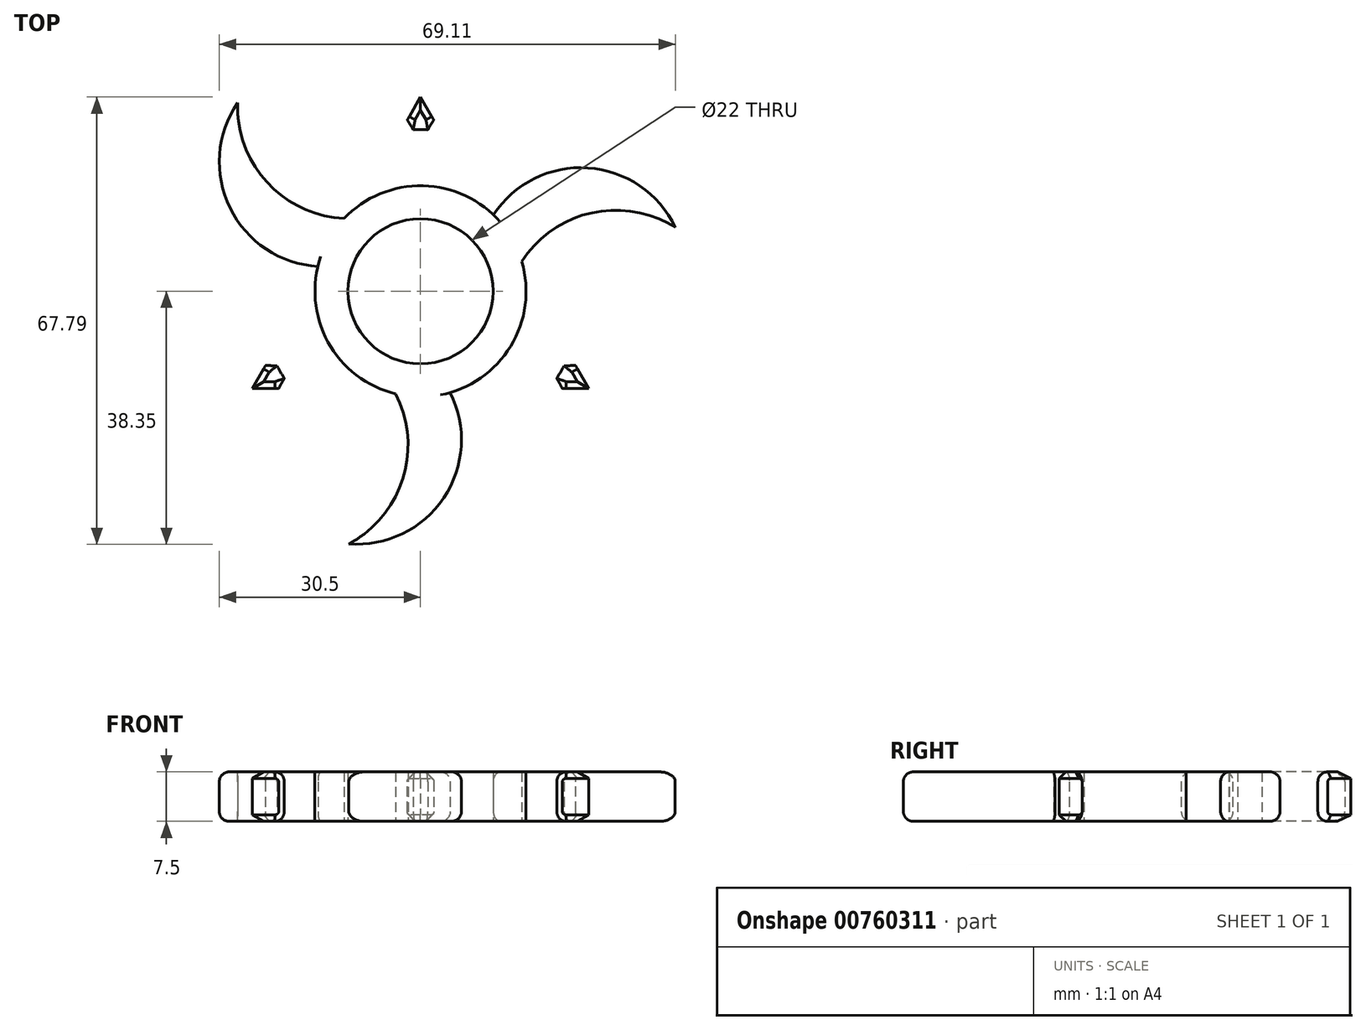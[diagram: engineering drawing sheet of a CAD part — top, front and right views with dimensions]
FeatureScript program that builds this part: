
annotation { "Feature Type Name" : "Feature", "Feature Type Description" : "" }
export const myFeature = defineFeature(function(context is Context, id is Id, definition is map)
    precondition{}
    {
        {
            var Q0;
            Q0=qCreatedBy(makeId("Top.planeOp"),FACE);
            var sketch = newSketch(context, id + "F0", { "sketchPlane" : qUnion([Q0])});
            skCircle(sketch, "E0", {"center": v(0, 0) * mm, "radius": 40 * mm, "construction": true});
            skLineSegment(sketch, "E1", {"start": v(-25.5, -14.72) * mm, "end": v(0, 29.44) * mm});
            skLineSegment(sketch, "E2", {"start": v(0, 29.44) * mm, "end": v(25.5, -14.72) * mm});
            skLineSegment(sketch, "E3", {"start": v(25.5, -14.72) * mm, "end": v(-25.5, -14.72) * mm});
            skCircle(sketch, "E4", {"center": v(0, 0) * mm, "radius": 11 * mm});
            skLineSegment(sketch, "E5", {"start": v(-25.5, -14.72) * mm, "end": v(0, 0) * mm, "construction": true});
            skLineSegment(sketch, "E6", {"start": v(0, 29.44) * mm, "end": v(0, 0) * mm, "construction": true});
            skLineSegment(sketch, "E7", {"start": v(0, 0) * mm, "end": v(25.5, -14.72) * mm, "construction": true});
            skCircle(sketch, "E8", {"center": v(0, 0) * mm, "radius": 16 * mm});
            skFitSpline(sketch, "E9", {"points": [v(7, -14.72) * mm, v(10.05, -23.38) * mm, v(9.77, -28.18) * mm, v(7.8, -33.41) * mm, v(4.12, -37.08) * mm, v(1.15, -38.78) * mm, v(-6.12, -39.53) * mm, v(-2.8, -36.94) * mm, v(2.56, -35.25) * mm, v(5.39, -31) * mm, v(2.14, -24.36) * mm, v(-7, -14.72) * mm], "startDerivative": vector(46.13, -62.16) * mm, "endDerivative": vector(-72.85, 54.12) * mm, "construction": true});
            skCircle(sketch, "E10", {"center": v(0, 0) * mm, "radius": 24.5 * mm});
            skCircle(sketch, "E11", {"center": v(0, 0) * mm, "radius": 20.5 * mm});
            skArc(sketch, "E12", {"start": v(-10.88, -38.3) * mm, "mid": v(3.51, -31.32) * mm, "end": v(4.5, -15.35) * mm});
            skArc(sketch, "E13.trimOffspring", {"start": v(-10.88, -38.3) * mm, "mid": v(-2.67, -28.38) * mm, "end": v(-3.76, -15.55) * mm});
            skArc(sketch, "E14.1.0", {"start": v(38.6, 9.73) * mm, "mid": v(25.37, 18.7) * mm, "end": v(11.04, 11.58) * mm});
            skArc(sketch, "E14.1.1", {"start": v(38.6, 9.73) * mm, "mid": v(25.91, 11.88) * mm, "end": v(15.35, 4.52) * mm});
            skArc(sketch, "E14.2.0", {"start": v(-27.73, 28.57) * mm, "mid": v(-28.88, 12.62) * mm, "end": v(-15.55, 3.77) * mm});
            skArc(sketch, "E14.2.1", {"start": v(-27.73, 28.57) * mm, "mid": v(-23.25, 16.5) * mm, "end": v(-11.59, 11.03) * mm});
            skSolve(sketch);
        }
        {
            var Q0;
            {var subQ0=sQuery(id+"F0.wireOp",EDGE,"E10");var subQ1=sQuery(id+"F0.wireOp",EDGE,"E3");var subQ2=makeQuery(id+"F0.imprint","INTERSECT",VERTEX,{"disambiguationData":[OD(0.0)],"derivedFrom":[subQ1,subQ0]});Q0=makeQuery(id+"F0.imprint","IMPRINT",FACE,{"disambiguationData":[TD([[makeQuery(id+"F0.imprint","IMPRINT",EDGE,{"disambiguationData":[TD([[subQ2,-1.0]])],"derivedFrom":subQ1}),1.0]])]});}
            var Q1;
            {var subQ0=sQuery(id+"F0.wireOp",EDGE,"E10");var subQ1=sQuery(id+"F0.wireOp",EDGE,"E3");var subQ2=makeQuery(id+"F0.imprint","INTERSECT",VERTEX,{"disambiguationData":[OD(1.0)],"derivedFrom":[subQ1,subQ0]});Q1=makeQuery(id+"F0.imprint","IMPRINT",FACE,{"disambiguationData":[TD([[makeQuery(id+"F0.imprint","IMPRINT",EDGE,{"disambiguationData":[TD([[subQ2,1.0]])],"derivedFrom":subQ1}),1.0]])]});}
            var Q2;
            {var subQ0=sQuery(id+"F0.wireOp",EDGE,"E8");var subQ1=sQuery(id+"F0.wireOp",EDGE,"E3");var subQ2=makeQuery(id+"F0.imprint","INTERSECT",VERTEX,{"disambiguationData":[OD(0.0)],"derivedFrom":[subQ1,subQ0]});Q2=makeQuery(id+"F0.imprint","IMPRINT",FACE,{"disambiguationData":[TD([[makeQuery(id+"F0.imprint","IMPRINT",EDGE,{"disambiguationData":[TD([[subQ2,-1.0]])],"derivedFrom":subQ1}),1.0]])]});}
            var Q3;
            {var subQ0=sQuery(id+"F0.wireOp",EDGE,"E3");var subQ1=sQuery(id+"F0.wireOp",EDGE,"E1");var subQ2=makeQuery(id+"F0.imprint","INTERSECT",VERTEX,{"derivedFrom":[subQ1,subQ0]});Q3=makeQuery(id+"F0.imprint","IMPRINT",FACE,{"disambiguationData":[TD([[makeQuery(id+"F0.imprint","IMPRINT",EDGE,{"disambiguationData":[TD([[subQ2,-1.0]])],"derivedFrom":subQ1}),-1.0]])]});}
            var Q4;
            {var subQ0=sQuery(id+"F0.wireOp",EDGE,"E10");var subQ1=sQuery(id+"F0.wireOp",EDGE,"E1");var subQ2=makeQuery(id+"F0.imprint","INTERSECT",VERTEX,{"disambiguationData":[OD(0.0)],"derivedFrom":[subQ1,subQ0]});Q4=makeQuery(id+"F0.imprint","IMPRINT",FACE,{"disambiguationData":[TD([[makeQuery(id+"F0.imprint","IMPRINT",EDGE,{"disambiguationData":[TD([[subQ2,-1.0]])],"derivedFrom":subQ1}),-1.0]])]});}
            var Q5;
            {var subQ0=sQuery(id+"F0.wireOp",EDGE,"E10");var subQ1=sQuery(id+"F0.wireOp",EDGE,"E1");var subQ2=makeQuery(id+"F0.imprint","INTERSECT",VERTEX,{"disambiguationData":[OD(0.0)],"derivedFrom":[subQ1,subQ0]});Q5=makeQuery(id+"F0.imprint","IMPRINT",FACE,{"disambiguationData":[TD([[makeQuery(id+"F0.imprint","IMPRINT",EDGE,{"disambiguationData":[TD([[subQ2,-1.0]])],"derivedFrom":subQ1}),1.0]])]});}
            var Q6;
            {var subQ0=sQuery(id+"F0.wireOp",EDGE,"E10");var subQ1=sQuery(id+"F0.wireOp",EDGE,"E1");var subQ2=makeQuery(id+"F0.imprint","INTERSECT",VERTEX,{"disambiguationData":[OD(1.0)],"derivedFrom":[subQ1,subQ0]});Q6=makeQuery(id+"F0.imprint","IMPRINT",FACE,{"disambiguationData":[TD([[makeQuery(id+"F0.imprint","IMPRINT",EDGE,{"disambiguationData":[TD([[subQ2,1.0]])],"derivedFrom":subQ1}),1.0]])]});}
            var Q7;
            {var subQ0=sQuery(id+"F0.wireOp",EDGE,"E2");var subQ1=sQuery(id+"F0.wireOp",EDGE,"E1");var subQ2=makeQuery(id+"F0.imprint","INTERSECT",VERTEX,{"derivedFrom":[subQ1,subQ0]});Q7=makeQuery(id+"F0.imprint","IMPRINT",FACE,{"disambiguationData":[TD([[makeQuery(id+"F0.imprint","IMPRINT",EDGE,{"disambiguationData":[TD([[subQ2,1.0]])],"derivedFrom":subQ1}),-1.0]])]});}
            var Q8;
            {var subQ0=sQuery(id+"F0.wireOp",EDGE,"E10");var subQ1=sQuery(id+"F0.wireOp",EDGE,"E1");var subQ2=makeQuery(id+"F0.imprint","INTERSECT",VERTEX,{"disambiguationData":[OD(1.0)],"derivedFrom":[subQ1,subQ0]});Q8=makeQuery(id+"F0.imprint","IMPRINT",FACE,{"disambiguationData":[TD([[makeQuery(id+"F0.imprint","IMPRINT",EDGE,{"disambiguationData":[TD([[subQ2,1.0]])],"derivedFrom":subQ1}),-1.0]])]});}
            var Q9;
            {var subQ0=sQuery(id+"F0.wireOp",EDGE,"E10");var subQ1=sQuery(id+"F0.wireOp",EDGE,"E2");var subQ2=makeQuery(id+"F0.imprint","INTERSECT",VERTEX,{"disambiguationData":[OD(0.0)],"derivedFrom":[subQ1,subQ0]});Q9=makeQuery(id+"F0.imprint","IMPRINT",FACE,{"disambiguationData":[TD([[makeQuery(id+"F0.imprint","IMPRINT",EDGE,{"disambiguationData":[TD([[subQ2,-1.0]])],"derivedFrom":subQ1}),1.0]])]});}
            var Q10;
            {var subQ0=sQuery(id+"F0.wireOp",EDGE,"E3");var subQ1=sQuery(id+"F0.wireOp",EDGE,"E2");var subQ2=makeQuery(id+"F0.imprint","INTERSECT",VERTEX,{"derivedFrom":[subQ1,subQ0]});Q10=makeQuery(id+"F0.imprint","IMPRINT",FACE,{"disambiguationData":[TD([[makeQuery(id+"F0.imprint","IMPRINT",EDGE,{"disambiguationData":[TD([[subQ2,1.0]])],"derivedFrom":subQ1}),-1.0]])]});}
            var Q11;
            {var subQ0=sQuery(id+"F0.wireOp",EDGE,"E10");var subQ1=sQuery(id+"F0.wireOp",EDGE,"E2");var subQ2=makeQuery(id+"F0.imprint","INTERSECT",VERTEX,{"disambiguationData":[OD(1.0)],"derivedFrom":[subQ1,subQ0]});Q11=makeQuery(id+"F0.imprint","IMPRINT",FACE,{"disambiguationData":[TD([[makeQuery(id+"F0.imprint","IMPRINT",EDGE,{"disambiguationData":[TD([[subQ2,1.0]])],"derivedFrom":subQ1}),-1.0]])]});}
            var Q12;
            {var subQ0=sQuery(id+"F0.wireOp",EDGE,"E10");var subQ1=sQuery(id+"F0.wireOp",EDGE,"E2");var subQ2=makeQuery(id+"F0.imprint","INTERSECT",VERTEX,{"disambiguationData":[OD(1.0)],"derivedFrom":[subQ1,subQ0]});Q12=makeQuery(id+"F0.imprint","IMPRINT",FACE,{"disambiguationData":[TD([[makeQuery(id+"F0.imprint","IMPRINT",EDGE,{"disambiguationData":[TD([[subQ2,1.0]])],"derivedFrom":subQ1}),1.0]])]});}
            var Q13;
            {var subQ0=sQuery(id+"F0.wireOp",EDGE,"E13.trimOffspring");var subQ1=sQuery(id+"F0.wireOp",EDGE,"E10");var subQ2=makeQuery(id+"F0.imprint","INTERSECT",VERTEX,{"derivedFrom":[subQ1,subQ0]});Q13=makeQuery(id+"F0.imprint","IMPRINT",FACE,{"disambiguationData":[TD([[makeQuery(id+"F0.imprint","IMPRINT",EDGE,{"disambiguationData":[TD([[subQ2,-1.0]])],"derivedFrom":subQ1}),-1.0]])]});}
            var Q14;
            {var subQ0=sQuery(id+"F0.wireOp",EDGE,"E13.trimOffspring");var subQ1=sQuery(id+"F0.wireOp",EDGE,"E10");var subQ2=makeQuery(id+"F0.imprint","INTERSECT",VERTEX,{"derivedFrom":[subQ1,subQ0]});Q14=makeQuery(id+"F0.imprint","IMPRINT",FACE,{"disambiguationData":[TD([[makeQuery(id+"F0.imprint","IMPRINT",EDGE,{"disambiguationData":[TD([[subQ2,-1.0]])],"derivedFrom":subQ1}),1.0]])]});}
            var Q15;
            {var subQ0=sQuery(id+"F0.wireOp",EDGE,"E14.1.0");var subQ1=sQuery(id+"F0.wireOp",EDGE,"E10");var subQ2=makeQuery(id+"F0.imprint","INTERSECT",VERTEX,{"derivedFrom":[subQ1,subQ0]});Q15=makeQuery(id+"F0.imprint","IMPRINT",FACE,{"disambiguationData":[TD([[makeQuery(id+"F0.imprint","IMPRINT",EDGE,{"disambiguationData":[TD([[subQ2,1.0]])],"derivedFrom":subQ1}),-1.0]])]});}
            var Q16;
            {var subQ0=sQuery(id+"F0.wireOp",EDGE,"E14.2.1");var subQ1=sQuery(id+"F0.wireOp",EDGE,"E10");var subQ2=makeQuery(id+"F0.imprint","INTERSECT",VERTEX,{"derivedFrom":[subQ1,subQ0]});Q16=makeQuery(id+"F0.imprint","IMPRINT",FACE,{"disambiguationData":[TD([[makeQuery(id+"F0.imprint","IMPRINT",EDGE,{"disambiguationData":[TD([[subQ2,-1.0]])],"derivedFrom":subQ1}),1.0]])]});}
            var Q17;
            {var subQ0=sQuery(id+"F0.wireOp",EDGE,"E14.2.1");var subQ1=sQuery(id+"F0.wireOp",EDGE,"E10");var subQ2=makeQuery(id+"F0.imprint","INTERSECT",VERTEX,{"derivedFrom":[subQ1,subQ0]});Q17=makeQuery(id+"F0.imprint","IMPRINT",FACE,{"disambiguationData":[TD([[makeQuery(id+"F0.imprint","IMPRINT",EDGE,{"disambiguationData":[TD([[subQ2,-1.0]])],"derivedFrom":subQ1}),-1.0]])]});}
            var Q18;
            {var subQ0=sQuery(id+"F0.wireOp",EDGE,"E8");var subQ1=sQuery(id+"F0.wireOp",EDGE,"E1");var subQ2=makeQuery(id+"F0.imprint","INTERSECT",VERTEX,{"disambiguationData":[OD(0.0)],"derivedFrom":[subQ1,subQ0]});Q18=makeQuery(id+"F0.imprint","IMPRINT",FACE,{"disambiguationData":[TD([[makeQuery(id+"F0.imprint","IMPRINT",EDGE,{"disambiguationData":[TD([[subQ2,-1.0]])],"derivedFrom":subQ1}),1.0]])]});}
            var Q19;
            {var subQ0=sQuery(id+"F0.wireOp",EDGE,"E8");var subQ1=sQuery(id+"F0.wireOp",EDGE,"E2");var subQ2=makeQuery(id+"F0.imprint","INTERSECT",VERTEX,{"disambiguationData":[OD(0.0)],"derivedFrom":[subQ1,subQ0]});Q19=makeQuery(id+"F0.imprint","IMPRINT",FACE,{"disambiguationData":[TD([[makeQuery(id+"F0.imprint","IMPRINT",EDGE,{"disambiguationData":[TD([[subQ2,-1.0]])],"derivedFrom":subQ1}),1.0]])]});}
            var Q20;
            Q20=makeQuery(id+"F0.imprint","IMPRINT",FACE,{"disambiguationData":[TD([[makeQuery(id+"F0.imprint","IMPRINT",EDGE,{"derivedFrom":sQuery(id+"F0.wireOp",EDGE,"E4")}),-1.0]])]});
            var Q21;
            {var subQ0=sQuery(id+"F0.wireOp",EDGE,"E14.1.0");var subQ1=sQuery(id+"F0.wireOp",EDGE,"E10");var subQ2=makeQuery(id+"F0.imprint","INTERSECT",VERTEX,{"derivedFrom":[subQ1,subQ0]});Q21=makeQuery(id+"F0.imprint","IMPRINT",FACE,{"disambiguationData":[TD([[makeQuery(id+"F0.imprint","IMPRINT",EDGE,{"disambiguationData":[TD([[subQ2,1.0]])],"derivedFrom":subQ1}),1.0]])]});}
            var Q22;
            {var subQ0=sQuery(id+"F0.wireOp",EDGE,"E12");var subQ1=sQuery(id+"F0.wireOp",EDGE,"E8");var subQ2=makeQuery(id+"F0.imprint","INTERSECT",VERTEX,{"derivedFrom":[subQ1,subQ0]});Q22=makeQuery(id+"F0.imprint","IMPRINT",FACE,{"disambiguationData":[TD([[makeQuery(id+"F0.imprint","IMPRINT",EDGE,{"disambiguationData":[TD([[subQ2,1.0]])],"derivedFrom":subQ1}),-1.0]])]});}
            var Q23;
            {var subQ0=sQuery(id+"F0.wireOp",EDGE,"E14.1.0");var subQ1=sQuery(id+"F0.wireOp",EDGE,"E8");var subQ2=makeQuery(id+"F0.imprint","INTERSECT",VERTEX,{"derivedFrom":[subQ1,subQ0]});Q23=makeQuery(id+"F0.imprint","IMPRINT",FACE,{"disambiguationData":[TD([[makeQuery(id+"F0.imprint","IMPRINT",EDGE,{"disambiguationData":[TD([[subQ2,1.0]])],"derivedFrom":subQ1}),-1.0]])]});}
            var Q24;
            {var subQ0=sQuery(id+"F0.wireOp",EDGE,"E14.2.0");var subQ1=sQuery(id+"F0.wireOp",EDGE,"E8");var subQ2=makeQuery(id+"F0.imprint","INTERSECT",VERTEX,{"derivedFrom":[subQ1,subQ0]});Q24=makeQuery(id+"F0.imprint","IMPRINT",FACE,{"disambiguationData":[TD([[makeQuery(id+"F0.imprint","IMPRINT",EDGE,{"disambiguationData":[TD([[subQ2,1.0]])],"derivedFrom":subQ1}),-1.0]])]});}
            extrude(context, id + "F1", {"entities" : qUnion([Q0, Q1, Q2, Q3, Q4, Q5, Q6, Q7, Q8, Q9, Q10, Q11, Q12, Q13, Q14, Q15, Q16, Q17, Q18, Q19, Q20, Q21, Q22, Q23, Q24]), "depth" : 7.5 * mm, "offsetDistance" : 25 * mm});
        }
        {
            var Q0;
            {var subQ0=sQuery(id+"F0.wireOp",EDGE,"E10");Q0=makeQuery(id+"F1.opExtrude","CAP_EDGE",EDGE,{"disambiguationData":[OSD([subQ0]),TDD([makeQuery(id+"F0.imprint","IMPRINT",EDGE,{"disambiguationData":[TD([[makeQuery(id+"F0.imprint","INTERSECT",VERTEX,{"disambiguationData":[OD(0.0)],"derivedFrom":[sQuery(id+"F0.wireOp",EDGE,"E1"),subQ0]}),1.0]])],"derivedFrom":subQ0})])],"isStart":true});}
            var Q1;
            {var subQ0=sQuery(id+"F0.wireOp",EDGE,"E10");Q1=makeQuery(id+"F1.opExtrude","CAP_EDGE",EDGE,{"disambiguationData":[OSD([subQ0]),TDD([makeQuery(id+"F0.imprint","IMPRINT",EDGE,{"disambiguationData":[TD([[makeQuery(id+"F0.imprint","INTERSECT",VERTEX,{"disambiguationData":[OD(1.0)],"derivedFrom":[sQuery(id+"F0.wireOp",EDGE,"E2"),subQ0]}),-1.0]])],"derivedFrom":subQ0})])],"isStart":true});}
            var Q2;
            {var subQ0=sQuery(id+"F0.wireOp",EDGE,"E10");Q2=makeQuery(id+"F1.opExtrude","CAP_EDGE",EDGE,{"disambiguationData":[OSD([subQ0]),TDD([makeQuery(id+"F0.imprint","IMPRINT",EDGE,{"disambiguationData":[TD([[makeQuery(id+"F0.imprint","INTERSECT",VERTEX,{"disambiguationData":[OD(1.0)],"derivedFrom":[sQuery(id+"F0.wireOp",EDGE,"E2"),subQ0]}),-1.0]])],"derivedFrom":subQ0})])],"isStart":false});}
            var Q3;
            {var subQ0=sQuery(id+"F0.wireOp",EDGE,"E10");Q3=makeQuery(id+"F1.opExtrude","CAP_EDGE",EDGE,{"disambiguationData":[OSD([subQ0]),TDD([makeQuery(id+"F0.imprint","IMPRINT",EDGE,{"disambiguationData":[TD([[makeQuery(id+"F0.imprint","INTERSECT",VERTEX,{"disambiguationData":[OD(1.0)],"derivedFrom":[sQuery(id+"F0.wireOp",EDGE,"E1"),subQ0]}),-1.0]])],"derivedFrom":subQ0})])],"isStart":false});}
            var Q4;
            {var subQ0=sQuery(id+"F0.wireOp",EDGE,"E10");Q4=makeQuery(id+"F1.opExtrude","CAP_EDGE",EDGE,{"disambiguationData":[OSD([subQ0]),TDD([makeQuery(id+"F0.imprint","IMPRINT",EDGE,{"disambiguationData":[TD([[makeQuery(id+"F0.imprint","INTERSECT",VERTEX,{"disambiguationData":[OD(1.0)],"derivedFrom":[sQuery(id+"F0.wireOp",EDGE,"E1"),subQ0]}),-1.0]])],"derivedFrom":subQ0})])],"isStart":true});}
            var Q5;
            {var subQ0=sQuery(id+"F0.wireOp",EDGE,"E10");Q5=makeQuery(id+"F1.opExtrude","CAP_EDGE",EDGE,{"disambiguationData":[OSD([subQ0]),TDD([makeQuery(id+"F0.imprint","IMPRINT",EDGE,{"disambiguationData":[TD([[makeQuery(id+"F0.imprint","INTERSECT",VERTEX,{"disambiguationData":[OD(0.0)],"derivedFrom":[sQuery(id+"F0.wireOp",EDGE,"E2"),subQ0]}),1.0]])],"derivedFrom":subQ0})])],"isStart":false});}
            var Q6;
            {var subQ0=sQuery(id+"F0.wireOp",EDGE,"E12");var subQ1=makeQuery(id+"F0.imprint","INTERSECT",VERTEX,{"derivedFrom":[sQuery(id+"F0.wireOp",EDGE,"E3"),subQ0]});Q6=makeQuery(id+"F1.opExtrude","CAP_EDGE",EDGE,{"disambiguationData":[OSD([subQ0]),TDD([makeQuery(id+"F0.imprint","IMPRINT",EDGE,{"disambiguationData":[TD([[subQ1,1.0]])],"derivedFrom":subQ0}),makeQuery(id+"F0.imprint","IMPRINT",EDGE,{"disambiguationData":[TD([[makeQuery(id+"F0.imprint","INTERSECT",VERTEX,{"derivedFrom":[sQuery(id+"F0.wireOp",EDGE,"E8"),subQ0]}),1.0]])],"derivedFrom":subQ0})])],"isStart":true});}
            var Q7;
            {var subQ0=sQuery(id+"F0.wireOp",EDGE,"E14.2.0");var subQ1=makeQuery(id+"F0.imprint","INTERSECT",VERTEX,{"derivedFrom":[sQuery(id+"F0.wireOp",EDGE,"E1"),subQ0]});Q7=makeQuery(id+"F1.opExtrude","CAP_EDGE",EDGE,{"disambiguationData":[OSD([subQ0]),TDD([makeQuery(id+"F0.imprint","IMPRINT",EDGE,{"disambiguationData":[TD([[subQ1,1.0]])],"derivedFrom":subQ0}),makeQuery(id+"F0.imprint","IMPRINT",EDGE,{"disambiguationData":[TD([[makeQuery(id+"F0.imprint","INTERSECT",VERTEX,{"derivedFrom":[sQuery(id+"F0.wireOp",EDGE,"E8"),subQ0]}),1.0]])],"derivedFrom":subQ0})])],"isStart":false});}
            var Q8;
            {var subQ0=sQuery(id+"F0.wireOp",EDGE,"E10");Q8=makeQuery(id+"F1.opExtrude","CAP_EDGE",EDGE,{"disambiguationData":[OSD([subQ0]),TDD([makeQuery(id+"F0.imprint","IMPRINT",EDGE,{"disambiguationData":[TD([[makeQuery(id+"F0.imprint","INTERSECT",VERTEX,{"disambiguationData":[OD(0.0)],"derivedFrom":[sQuery(id+"F0.wireOp",EDGE,"E1"),subQ0]}),1.0]])],"derivedFrom":subQ0})])],"isStart":false});}
            var Q9;
            {var subQ0=sQuery(id+"F0.wireOp",EDGE,"E10");Q9=makeQuery(id+"F1.opExtrude","CAP_EDGE",EDGE,{"disambiguationData":[OSD([subQ0]),TDD([makeQuery(id+"F0.imprint","IMPRINT",EDGE,{"disambiguationData":[TD([[makeQuery(id+"F0.imprint","INTERSECT",VERTEX,{"disambiguationData":[OD(1.0)],"derivedFrom":[sQuery(id+"F0.wireOp",EDGE,"E3"),subQ0]}),-1.0]])],"derivedFrom":subQ0})])],"isStart":false});}
            var Q10;
            {var subQ0=sQuery(id+"F0.wireOp",EDGE,"E10");Q10=makeQuery(id+"F1.opExtrude","CAP_EDGE",EDGE,{"disambiguationData":[OSD([subQ0]),TDD([makeQuery(id+"F0.imprint","IMPRINT",EDGE,{"disambiguationData":[TD([[makeQuery(id+"F0.imprint","INTERSECT",VERTEX,{"disambiguationData":[OD(1.0)],"derivedFrom":[sQuery(id+"F0.wireOp",EDGE,"E3"),subQ0]}),-1.0]])],"derivedFrom":subQ0})])],"isStart":true});}
            var Q11;
            {var subQ0=sQuery(id+"F0.wireOp",EDGE,"E10");Q11=makeQuery(id+"F1.opExtrude","CAP_EDGE",EDGE,{"disambiguationData":[OSD([subQ0]),TDD([makeQuery(id+"F0.imprint","IMPRINT",EDGE,{"disambiguationData":[TD([[makeQuery(id+"F0.imprint","INTERSECT",VERTEX,{"disambiguationData":[OD(0.0)],"derivedFrom":[sQuery(id+"F0.wireOp",EDGE,"E3"),subQ0]}),1.0]])],"derivedFrom":subQ0})])],"isStart":false});}
            var Q12;
            {var subQ0=sQuery(id+"F0.wireOp",EDGE,"E10");Q12=makeQuery(id+"F1.opExtrude","CAP_EDGE",EDGE,{"disambiguationData":[OSD([subQ0]),TDD([makeQuery(id+"F0.imprint","IMPRINT",EDGE,{"disambiguationData":[TD([[makeQuery(id+"F0.imprint","INTERSECT",VERTEX,{"disambiguationData":[OD(0.0)],"derivedFrom":[sQuery(id+"F0.wireOp",EDGE,"E3"),subQ0]}),1.0]])],"derivedFrom":subQ0})])],"isStart":true});}
            var Q13;
            {var subQ0=sQuery(id+"F0.wireOp",EDGE,"E12");Q13=makeQuery(id+"F1.opExtrude","CAP_EDGE",EDGE,{"disambiguationData":[OSD([subQ0]),TDD([makeQuery(id+"F0.imprint","IMPRINT",EDGE,{"disambiguationData":[TD([[makeQuery(id+"F0.imprint","INTERSECT",VERTEX,{"derivedFrom":[subQ0,sQuery(id+"F0.wireOp",EDGE,"E13.trimOffspring")]}),-1.0]])],"derivedFrom":subQ0})])],"isStart":false});}
            var Q14;
            {var subQ0=sQuery(id+"F0.wireOp",EDGE,"E12");Q14=makeQuery(id+"F1.opExtrude","CAP_EDGE",EDGE,{"disambiguationData":[OSD([subQ0]),TDD([makeQuery(id+"F0.imprint","IMPRINT",EDGE,{"disambiguationData":[TD([[makeQuery(id+"F0.imprint","INTERSECT",VERTEX,{"derivedFrom":[subQ0,sQuery(id+"F0.wireOp",EDGE,"E13.trimOffspring")]}),-1.0]])],"derivedFrom":subQ0})])],"isStart":true});}
            var Q15;
            {var subQ0=sQuery(id+"F0.wireOp",EDGE,"E14.2.0");Q15=makeQuery(id+"F1.opExtrude","CAP_EDGE",EDGE,{"disambiguationData":[OSD([subQ0]),TDD([makeQuery(id+"F0.imprint","IMPRINT",EDGE,{"disambiguationData":[TD([[makeQuery(id+"F0.imprint","INTERSECT",VERTEX,{"derivedFrom":[subQ0,sQuery(id+"F0.wireOp",EDGE,"E14.2.1")]}),-1.0]])],"derivedFrom":subQ0})])],"isStart":false});}
            var Q16;
            {var subQ0=sQuery(id+"F0.wireOp",EDGE,"E14.2.0");Q16=makeQuery(id+"F1.opExtrude","CAP_EDGE",EDGE,{"disambiguationData":[OSD([subQ0]),TDD([makeQuery(id+"F0.imprint","IMPRINT",EDGE,{"disambiguationData":[TD([[makeQuery(id+"F0.imprint","INTERSECT",VERTEX,{"derivedFrom":[subQ0,sQuery(id+"F0.wireOp",EDGE,"E14.2.1")]}),-1.0]])],"derivedFrom":subQ0})])],"isStart":true});}
            var Q17;
            {var subQ0=sQuery(id+"F0.wireOp",EDGE,"E14.1.0");Q17=makeQuery(id+"F1.opExtrude","CAP_EDGE",EDGE,{"disambiguationData":[OSD([subQ0]),TDD([makeQuery(id+"F0.imprint","IMPRINT",EDGE,{"disambiguationData":[TD([[makeQuery(id+"F0.imprint","INTERSECT",VERTEX,{"derivedFrom":[subQ0,sQuery(id+"F0.wireOp",EDGE,"E14.1.1")]}),-1.0]])],"derivedFrom":subQ0})])],"isStart":true});}
            var Q18;
            {var subQ0=sQuery(id+"F0.wireOp",EDGE,"E14.1.0");Q18=makeQuery(id+"F1.opExtrude","CAP_EDGE",EDGE,{"disambiguationData":[OSD([subQ0]),TDD([makeQuery(id+"F0.imprint","IMPRINT",EDGE,{"disambiguationData":[TD([[makeQuery(id+"F0.imprint","INTERSECT",VERTEX,{"derivedFrom":[subQ0,sQuery(id+"F0.wireOp",EDGE,"E14.1.1")]}),-1.0]])],"derivedFrom":subQ0})])],"isStart":false});}
            var Q19;
            {var subQ0=sQuery(id+"F0.wireOp",EDGE,"E10");Q19=makeQuery(id+"F1.opExtrude","CAP_EDGE",EDGE,{"disambiguationData":[OSD([subQ0]),TDD([makeQuery(id+"F0.imprint","IMPRINT",EDGE,{"disambiguationData":[TD([[makeQuery(id+"F0.imprint","INTERSECT",VERTEX,{"disambiguationData":[OD(0.0)],"derivedFrom":[sQuery(id+"F0.wireOp",EDGE,"E2"),subQ0]}),1.0]])],"derivedFrom":subQ0})])],"isStart":true});}
            var Q20;
            {var subQ0=sQuery(id+"F0.wireOp",EDGE,"E12");var subQ1=makeQuery(id+"F0.imprint","INTERSECT",VERTEX,{"derivedFrom":[sQuery(id+"F0.wireOp",EDGE,"E3"),subQ0]});Q20=makeQuery(id+"F1.opExtrude","CAP_EDGE",EDGE,{"disambiguationData":[OSD([subQ0]),TDD([makeQuery(id+"F0.imprint","IMPRINT",EDGE,{"disambiguationData":[TD([[subQ1,1.0]])],"derivedFrom":subQ0}),makeQuery(id+"F0.imprint","IMPRINT",EDGE,{"disambiguationData":[TD([[makeQuery(id+"F0.imprint","INTERSECT",VERTEX,{"derivedFrom":[sQuery(id+"F0.wireOp",EDGE,"E8"),subQ0]}),1.0]])],"derivedFrom":subQ0})])],"isStart":false});}
            var Q21;
            {var subQ0=sQuery(id+"F0.wireOp",EDGE,"E14.2.0");var subQ1=makeQuery(id+"F0.imprint","INTERSECT",VERTEX,{"derivedFrom":[sQuery(id+"F0.wireOp",EDGE,"E1"),subQ0]});Q21=makeQuery(id+"F1.opExtrude","CAP_EDGE",EDGE,{"disambiguationData":[OSD([subQ0]),TDD([makeQuery(id+"F0.imprint","IMPRINT",EDGE,{"disambiguationData":[TD([[subQ1,1.0]])],"derivedFrom":subQ0}),makeQuery(id+"F0.imprint","IMPRINT",EDGE,{"disambiguationData":[TD([[makeQuery(id+"F0.imprint","INTERSECT",VERTEX,{"derivedFrom":[sQuery(id+"F0.wireOp",EDGE,"E8"),subQ0]}),1.0]])],"derivedFrom":subQ0})])],"isStart":true});}
            var Q22;
            {var subQ0=sQuery(id+"F0.wireOp",EDGE,"E14.1.0");var subQ1=makeQuery(id+"F0.imprint","INTERSECT",VERTEX,{"derivedFrom":[sQuery(id+"F0.wireOp",EDGE,"E2"),subQ0]});Q22=makeQuery(id+"F1.opExtrude","CAP_EDGE",EDGE,{"disambiguationData":[OSD([subQ0]),TDD([makeQuery(id+"F0.imprint","IMPRINT",EDGE,{"disambiguationData":[TD([[subQ1,1.0]])],"derivedFrom":subQ0}),makeQuery(id+"F0.imprint","IMPRINT",EDGE,{"disambiguationData":[TD([[makeQuery(id+"F0.imprint","INTERSECT",VERTEX,{"derivedFrom":[sQuery(id+"F0.wireOp",EDGE,"E8"),subQ0]}),1.0]])],"derivedFrom":subQ0})])],"isStart":true});}
            var Q23;
            {var subQ0=sQuery(id+"F0.wireOp",EDGE,"E14.1.0");var subQ1=makeQuery(id+"F0.imprint","INTERSECT",VERTEX,{"derivedFrom":[sQuery(id+"F0.wireOp",EDGE,"E2"),subQ0]});Q23=makeQuery(id+"F1.opExtrude","CAP_EDGE",EDGE,{"disambiguationData":[OSD([subQ0]),TDD([makeQuery(id+"F0.imprint","IMPRINT",EDGE,{"disambiguationData":[TD([[subQ1,1.0]])],"derivedFrom":subQ0}),makeQuery(id+"F0.imprint","IMPRINT",EDGE,{"disambiguationData":[TD([[makeQuery(id+"F0.imprint","INTERSECT",VERTEX,{"derivedFrom":[sQuery(id+"F0.wireOp",EDGE,"E8"),subQ0]}),1.0]])],"derivedFrom":subQ0})])],"isStart":false});}
            fillet(context, id + "F2", {"entities" : qUnion([Q0, Q1, Q2, Q3, Q4, Q5, Q6, Q7, Q8, Q9, Q10, Q11, Q12, Q13, Q14, Q15, Q16, Q17, Q18, Q19, Q20, Q21, Q22, Q23]), "radius" : 1.5 * mm, "tangentPropagation" : true, "allowEdgeOverflow" : false});
        }
        {
            var Q0;
            Q0=makeQuery(id+"F1.opExtrude","CAP_EDGE",EDGE,{"disambiguationData":[OSD([sQuery(id+"F0.wireOp",EDGE,"66d0fcba-591a-4f48-91e7-a478066faa3b.2.2")])],"isStart":false});
            var Q1;
            Q1=makeQuery(id+"F1.opExtrude","SWEPT_FACE",FACE,{"disambiguationData":[OSD([sQuery(id+"F0.wireOp",EDGE,"66d0fcba-591a-4f48-91e7-a478066faa3b.2.2")])]});
            var Q2;
            {var subQ0=sQuery(id+"F0.wireOp",EDGE,"E3");Q2=makeQuery(id+"F1.opExtrude","CAP_EDGE",EDGE,{"disambiguationData":[OSD([subQ0]),TDD([makeQuery(id+"F0.imprint","IMPRINT",EDGE,{"disambiguationData":[TD([[makeQuery(id+"F0.imprint","INTERSECT",VERTEX,{"derivedFrom":[sQuery(id+"F0.wireOp",EDGE,"E2"),subQ0]}),-1.0]])],"derivedFrom":subQ0})])],"isStart":false});}
            var Q3;
            {var subQ0=sQuery(id+"F0.wireOp",EDGE,"E2");Q3=makeQuery(id+"F1.opExtrude","CAP_EDGE",EDGE,{"disambiguationData":[OSD([subQ0]),TDD([makeQuery(id+"F0.imprint","IMPRINT",EDGE,{"disambiguationData":[TD([[makeQuery(id+"F0.imprint","INTERSECT",VERTEX,{"derivedFrom":[subQ0,sQuery(id+"F0.wireOp",EDGE,"E3")]}),1.0]])],"derivedFrom":subQ0})])],"isStart":false});}
            var Q4;
            {var subQ0=sQuery(id+"F0.wireOp",EDGE,"E3");Q4=makeQuery(id+"F1.opExtrude","CAP_EDGE",EDGE,{"disambiguationData":[OSD([subQ0]),TDD([makeQuery(id+"F0.imprint","IMPRINT",EDGE,{"disambiguationData":[TD([[makeQuery(id+"F0.imprint","INTERSECT",VERTEX,{"derivedFrom":[sQuery(id+"F0.wireOp",EDGE,"E2"),subQ0]}),-1.0]])],"derivedFrom":subQ0})])],"isStart":true});}
            var Q5;
            {var subQ0=sQuery(id+"F0.wireOp",EDGE,"E2");Q5=makeQuery(id+"F1.opExtrude","CAP_EDGE",EDGE,{"disambiguationData":[OSD([subQ0]),TDD([makeQuery(id+"F0.imprint","IMPRINT",EDGE,{"disambiguationData":[TD([[makeQuery(id+"F0.imprint","INTERSECT",VERTEX,{"derivedFrom":[subQ0,sQuery(id+"F0.wireOp",EDGE,"E3")]}),1.0]])],"derivedFrom":subQ0})])],"isStart":true});}
            var Q6;
            {var subQ0=sQuery(id+"F0.wireOp",EDGE,"E1");Q6=makeQuery(id+"F1.opExtrude","CAP_EDGE",EDGE,{"disambiguationData":[OSD([subQ0]),TDD([makeQuery(id+"F0.imprint","IMPRINT",EDGE,{"disambiguationData":[TD([[makeQuery(id+"F0.imprint","INTERSECT",VERTEX,{"derivedFrom":[subQ0,sQuery(id+"F0.wireOp",EDGE,"E3")]}),-1.0]])],"derivedFrom":subQ0})])],"isStart":true});}
            var Q7;
            {var subQ0=sQuery(id+"F0.wireOp",EDGE,"E3");Q7=makeQuery(id+"F1.opExtrude","CAP_EDGE",EDGE,{"disambiguationData":[OSD([subQ0]),TDD([makeQuery(id+"F0.imprint","IMPRINT",EDGE,{"disambiguationData":[TD([[makeQuery(id+"F0.imprint","INTERSECT",VERTEX,{"derivedFrom":[sQuery(id+"F0.wireOp",EDGE,"E1"),subQ0]}),1.0]])],"derivedFrom":subQ0})])],"isStart":true});}
            var Q8;
            {var subQ0=sQuery(id+"F0.wireOp",EDGE,"E3");Q8=makeQuery(id+"F1.opExtrude","CAP_EDGE",EDGE,{"disambiguationData":[OSD([subQ0]),TDD([makeQuery(id+"F0.imprint","IMPRINT",EDGE,{"disambiguationData":[TD([[makeQuery(id+"F0.imprint","INTERSECT",VERTEX,{"derivedFrom":[sQuery(id+"F0.wireOp",EDGE,"E1"),subQ0]}),1.0]])],"derivedFrom":subQ0})])],"isStart":false});}
            var Q9;
            {var subQ0=sQuery(id+"F0.wireOp",EDGE,"E1");Q9=makeQuery(id+"F1.opExtrude","CAP_EDGE",EDGE,{"disambiguationData":[OSD([subQ0]),TDD([makeQuery(id+"F0.imprint","IMPRINT",EDGE,{"disambiguationData":[TD([[makeQuery(id+"F0.imprint","INTERSECT",VERTEX,{"derivedFrom":[subQ0,sQuery(id+"F0.wireOp",EDGE,"E3")]}),-1.0]])],"derivedFrom":subQ0})])],"isStart":false});}
            var Q10;
            {var subQ0=sQuery(id+"F0.wireOp",EDGE,"E1");Q10=makeQuery(id+"F1.opExtrude","CAP_EDGE",EDGE,{"disambiguationData":[OSD([subQ0]),TDD([makeQuery(id+"F0.imprint","IMPRINT",EDGE,{"disambiguationData":[TD([[makeQuery(id+"F0.imprint","INTERSECT",VERTEX,{"derivedFrom":[subQ0,sQuery(id+"F0.wireOp",EDGE,"E2")]}),1.0]])],"derivedFrom":subQ0})])],"isStart":true});}
            var Q11;
            {var subQ0=sQuery(id+"F0.wireOp",EDGE,"E2");Q11=makeQuery(id+"F1.opExtrude","CAP_EDGE",EDGE,{"disambiguationData":[OSD([subQ0]),TDD([makeQuery(id+"F0.imprint","IMPRINT",EDGE,{"disambiguationData":[TD([[makeQuery(id+"F0.imprint","INTERSECT",VERTEX,{"derivedFrom":[sQuery(id+"F0.wireOp",EDGE,"E1"),subQ0]}),-1.0]])],"derivedFrom":subQ0})])],"isStart":true});}
            var Q12;
            {var subQ0=sQuery(id+"F0.wireOp",EDGE,"E2");Q12=makeQuery(id+"F1.opExtrude","CAP_EDGE",EDGE,{"disambiguationData":[OSD([subQ0]),TDD([makeQuery(id+"F0.imprint","IMPRINT",EDGE,{"disambiguationData":[TD([[makeQuery(id+"F0.imprint","INTERSECT",VERTEX,{"derivedFrom":[sQuery(id+"F0.wireOp",EDGE,"E1"),subQ0]}),-1.0]])],"derivedFrom":subQ0})])],"isStart":false});}
            var Q13;
            {var subQ0=sQuery(id+"F0.wireOp",EDGE,"E1");Q13=makeQuery(id+"F1.opExtrude","CAP_EDGE",EDGE,{"disambiguationData":[OSD([subQ0]),TDD([makeQuery(id+"F0.imprint","IMPRINT",EDGE,{"disambiguationData":[TD([[makeQuery(id+"F0.imprint","INTERSECT",VERTEX,{"derivedFrom":[subQ0,sQuery(id+"F0.wireOp",EDGE,"E2")]}),1.0]])],"derivedFrom":subQ0})])],"isStart":false});}
            chamfer(context, id + "F3", {"entities" : qUnion([Q0, Q1, Q2, Q3, Q4, Q5, Q6, Q7, Q8, Q9, Q10, Q11, Q12, Q13]), "width" : 1 * mm, "tangentPropagation" : true});
        }
    });
